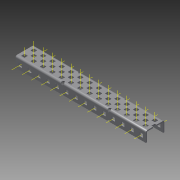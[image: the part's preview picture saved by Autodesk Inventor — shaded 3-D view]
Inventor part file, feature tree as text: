
AUTODESK INVENTOR PART (.ipt)
format: ipt  version: 2015 (Build 190159000, 159)  size: 2,060,800 bytes
history: native  units: in
note: dims shown in document units (in); Inventor stores cm internally (conversion verified against a paired STEP export)
features: other x76, pattern_linear x3, sheet_metal_op x1, extrude x1, imported_body x1, sketch x1
ambient origin geometry x8: Origin, YZ Plane, XZ Plane, XY Plane, X Axis, Y Axis, Z Axis, Center Point
bodies: Body1 (feature_tree)
feature tree (83):
  sheet_metal_op  "Fold1"
  other  "C-Channel"
  extrude  "length cut"  Depth=0.5in
  other  "top axis"
  other  "inner axis"
  other  "front axis"
  other  "back axis"
  pattern_linear  "top axes"  Spacing1=0.5in  [1 undecoded]
  pattern_linear  "inner axes"  Spacing1=0.5in  [1 undecoded]
  pattern_linear  "horiz axes"  Spacing1=-7.0in  [1 undecoded]
  other  "right plane"
  imported_body  "Base1"
  sketch  "Sketch1"  dims[d1=0.0in d4=0.5in d5=0.7874in d7=0.5in d10=0.5in d13=0.5in d14=-7.0in d15=0.0in d16=0.0in d17=0.0in d18=0.0in d19=0.0in]
  other  "Work Point1"
  other  "Work Point2"
  other  "Work Point3"
  other  "Work Point4"
  other  "Work Axis5"
  other  "Work Axis6"
  other  "Work Axis7"
  other  "Work Axis8"
  other  "Work Axis11"
  other  "Work Axis12"
  other  "Work Axis13"
  other  "Work Axis14"
  other  "Work Axis15"
  other  "Work Axis18"
  other  "Work Axis19"
  other  "Work Axis20"
  other  "Work Axis23"
  other  "Work Axis24"
  other  "Work Axis25"
  other  "Work Axis26"
  other  "Work Axis30"
  other  "Work Axis31"
  other  "Work Axis32"
  other  "Work Axis33"
  other  "left plane"
  other  "Work Axis37"
  other  "Work Axis38"
  other  "Work Axis39"
  other  "Work Axis40"
  other  "Work Axis41"
  other  "Work Axis42"
  other  "Work Axis43"
  other  "Work Axis44"
  other  "Work Axis45"
  other  "Work Axis57"
  other  "Work Axis58"
  other  "Work Axis59"
  other  "Work Axis60"
  other  "Work Axis61"
  other  "Work Axis62"
  other  "Work Axis63"
  other  "Work Axis64"
  other  "Work Axis65"
  other  "Work Axis77"
  other  "Work Axis78"
  other  "Work Axis79"
  other  "Work Axis80"
  other  "Work Axis81"
  other  "Work Axis82"
  other  "Work Axis83"
  other  "Work Axis84"
  other  "Work Axis85"
  other  "Work Axis97"
  other  "Work Axis98"
  other  "Work Axis99"
  other  "Work Axis100"
  other  "Work Axis101"
  other  "Work Axis102"
  other  "Work Axis103"
  other  "Work Axis104"
  other  "Work Axis105"
  other  "Work Axis117"
  other  "Work Axis118"
  other  "Work Axis119"
  other  "Work Axis120"
  other  "Work Axis121"
  other  "Work Axis122"
  other  "Work Axis123"
  other  "Work Axis124"
  other  "Work Axis125"
note: 3 required parameter values undecoded (feature->parameter linkage not recoverable at this tier; creation-order binding heuristic only, values carry confidence <= 0.55)
